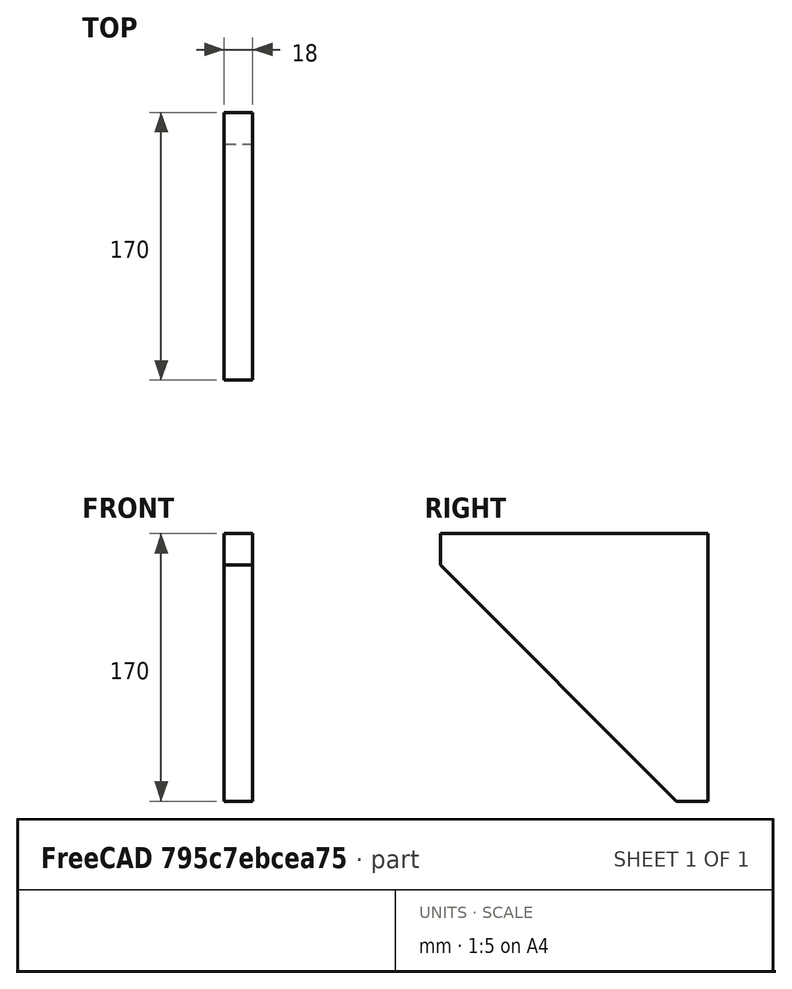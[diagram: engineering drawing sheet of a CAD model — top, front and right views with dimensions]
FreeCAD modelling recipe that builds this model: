
FCSTD DOCUMENT  (FreeCAD 0.18R4 (GitTag))
Label: side
License: All rights reserved
LicenseURL: http://en.wikipedia.org/wiki/All_rights_reserved
objects: Sketcher::SketchObject×1, PartDesign::Pad×1, PartDesign::Body×1
note: 4 computed .brp shape members not serialized (recipe doc carries the construction recipe); baked Part::Feature solids carry a one-line shape summary decoded from their .brp

FEATURE [Sketcher::SketchObject] Sketch
  MapMode = 5
  Placement = pos=(0,0,0) rot=(0.57735,0.57735,0.57735;2.0944rad)
  Support = -> [YZ_Plane]
  sketch-geometry (5):
    g0: LineSegment StartX=0 StartY=170 StartZ=0 EndX=-170 EndY=170 EndZ=0
    g1: LineSegment StartX=-170 StartY=170 StartZ=0 EndX=-170 EndY=150 EndZ=0
    g2: LineSegment StartX=-170 StartY=150 StartZ=0 EndX=-20 EndY=0 EndZ=0
    g3: LineSegment StartX=-20 StartY=0 StartZ=0 EndX=0 EndY=0 EndZ=0
    g4: LineSegment StartX=0 StartY=0 StartZ=0 EndX=0 EndY=170 EndZ=0
  constraints (14):
    c: Coincident(g4,g0)
    c: Coincident(g1,g0)
    c: Coincident(g1,g2)
    c: Coincident(g2,g3)
    c: Coincident(g3,g4)
    c: Horizontal(g0)
    c: Horizontal(g3)
    c: Vertical(g4)
    c: Vertical(g1)
    c: Coincident(g3,g-1)
    c: DistanceY(g4,g4) = 170
    c: DistanceX(g0,g0) = 170
    c: DistanceY(g1,g1) = 20
    c: DistanceX(g3,g3) = 20
FEATURE [PartDesign::Pad] Pad
  Length = 18
  Length2 = 100
  Placement = pos=(0,0,0) rot=(0.57735,0.57735,0.57735;2.0944rad)
  Profile = -> Sketch
  Type = 0
FEATURE [PartDesign::Body] Body
  Group = -> [Sketch,Pad]
  Origin = -> Origin
  Tip = -> Pad
